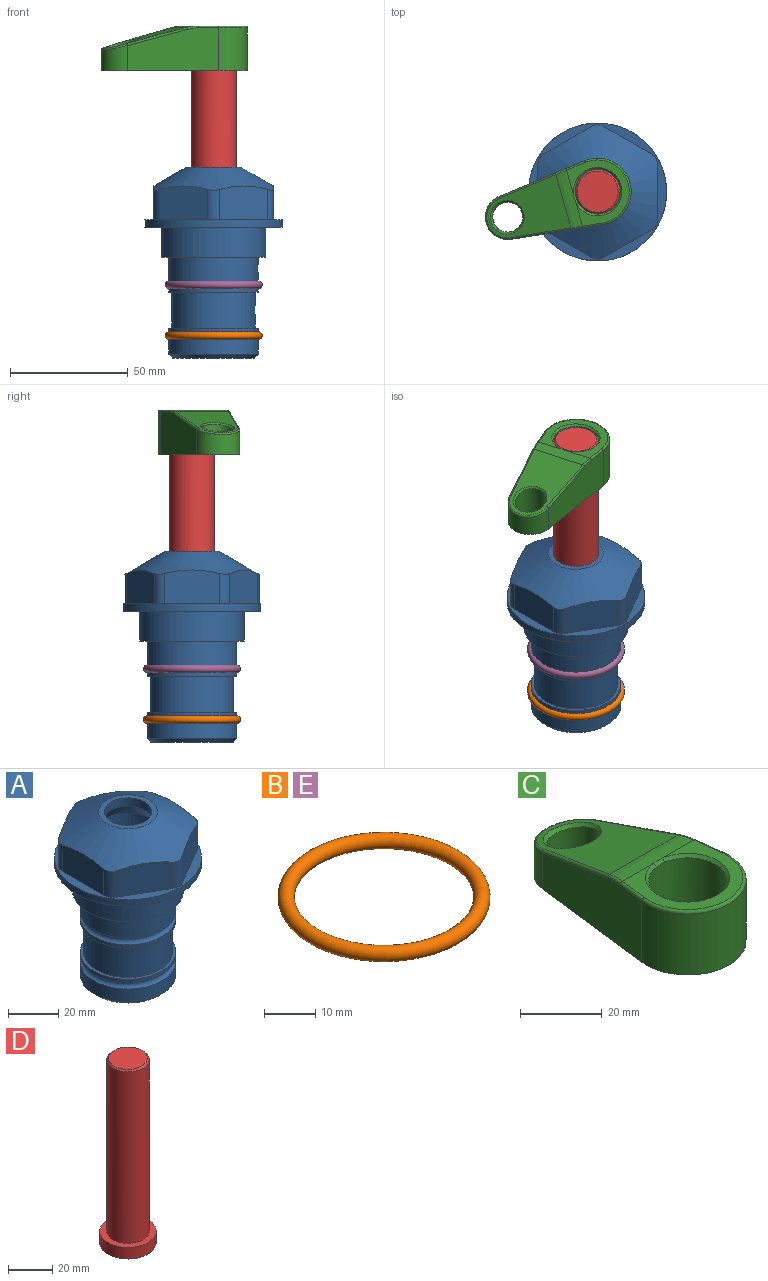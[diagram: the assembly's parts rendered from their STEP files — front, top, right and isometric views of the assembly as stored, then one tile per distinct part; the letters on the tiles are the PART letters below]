
ASSEMBLY  parts=5 mates=4
PART A: 36 faces, bbox 58.7x58.7x81 mm
  f0: cylinder r=17.78mm len=35.56mm, axis (0,0,1), area 1670.8mm2, adj f23,f24,f31
  f1: cylinder r=19.05mm len=38.1mm, axis (0,0,1), area 1191.9mm2, adj f26,f27,f30
  f2: plane 58.66x58.66mm, normal (0,0,-1), area 1150.6mm2, adj f3,f28
  f3: cylinder r=29.33mm len=58.66mm, axis (0,0,-1), area 585.1mm2, adj f2,f4
  f4: plane 58.66x58.66mm, normal (0,0,1), area 475.9mm2, adj f3,f5,f6,f7,f8,f9,f10,f11
  f5: plane 20.32x14.34mm, normal (-0.5,0.87,0), area 324.4mm2, adj f4,f15,f16,f17
  f6: plane 20.32x14.34mm, normal (0.5,0.87,0), area 324.4mm2, adj f4,f14,f15,f17
  f7: plane 23.48x14.34mm, normal (1,0,0), area 324.4mm2, adj f4,f13,f14,f17
  f8: plane 20.32x14.34mm, normal (0.5,-0.87,0), area 324.4mm2, adj f4,f12,f13,f17
  f9: plane 20.32x14.34mm, normal (-0.5,-0.87,0), area 324.4mm2, adj f4,f11,f12,f17
  f10: plane 23.48x14.34mm, normal (-1,0,0), area 324.4mm2, adj f4,f11,f16,f17
  f11: cylinder r=5.08mm len=12.85mm, axis (0,0,-1), area 67.2mm2, adj f4,f9,f10,f17
  f12: cylinder r=5.08mm len=12.85mm, axis (0,0,-1), area 67.2mm2, adj f4,f8,f9,f17
  f13: cylinder r=5.08mm len=12.85mm, axis (0,0,-1), area 67.2mm2, adj f4,f7,f8,f17
  f14: cylinder r=5.08mm len=12.85mm, axis (0,0,-1), area 67.2mm2, adj f4,f6,f7,f17
  f15: cylinder r=5.08mm len=12.85mm, axis (0,0,-1), area 67.2mm2, adj f4,f5,f6,f17
  f16: cylinder r=5.08mm len=12.85mm, axis (0,0,-1), area 67.2mm2, adj f4,f5,f10,f17
  f17: cone r=11.73mm half-angle=60deg, axis (0,0,-1), area 2071.8mm2, adj f5,f6,f7,f8,f9,f10,f11,f12
  f18: plane 23.46x23.46mm, normal (0,0,1), area 147.4mm2, adj f17,f35
  f19: plane 34.93x34.93mm, normal (0,0,-1), area 958mm2, adj f29
  f20: cylinder r=19.05mm len=38.1mm, axis (0,0,1), area 760.1mm2, adj f21,f29
  f21: torus R=19.05mm, axis (0,0,1), area 565.3mm2, adj f20,f22
  f22: cylinder r=19.05mm len=38.1mm, axis (0,0,1), area 190mm2, adj f21,f23
  f23: plane 38.1x38.1mm, normal (0,0,1), area 146.9mm2, adj f0,f22
  f24: plane 38.1x38.1mm, normal (0,0,-1), area 146.9mm2, adj f0,f25
  f25: cylinder r=19.05mm len=38.1mm, axis (0,0,1), area 190mm2, adj f24,f26
  f26: torus R=19.05mm, axis (0,0,1), area 565.3mm2, adj f1,f25
  f27: plane 44.45x44.45mm, normal (0,0,-1), area 411.7mm2, adj f1,f28
  f28: cylinder r=22.23mm len=44.45mm, axis (0,0,1), area 1773.5mm2, adj f2,f27
  f29: cone r=19.05mm half-angle=45deg, axis (0,0,1), area 257.5mm2, adj f19,f20
  f30: cylinder r=3.17mm len=6.75mm, axis (-1,0,0), area 128mm2, adj f1,f33
  f31: cylinder r=3.17mm len=6.35mm, axis (-1,0,0), area 102.5mm2, adj f0,f33
  f32: plane 25.4x25.4mm, normal (0,0,1), area 506.7mm2, adj f33
  f33: cylinder r=12.7mm len=66.42mm, axis (0,0,-1), area 5236.2mm2, adj f30,f31,f32,f34
  f34: cone r=9.53mm half-angle=30deg, axis (0,0,-1), area 443.4mm2, adj f33,f35
  f35: cylinder r=9.53mm len=19.05mm, axis (0,0,-1), area 240.9mm2, adj f18,f34
PART B: 1 faces, bbox 44.7x44.7x3.2 mm
  f0: torus R=19.05mm, axis (0,0,1), area 1193.9mm2
PART C: 31 faces, bbox 31.7x65.5x19.8 mm
  f0: plane 39.12x18.26mm, normal (0.99,0.12,0), area 612.2mm2, adj f1,f4,f7,f11,f13,f15
  f1: cylinder r=9.53mm len=18.91mm, axis (0,0,-1), area 296.1mm2, adj f0,f2,f7,f17
  f2: plane 39.12x18.26mm, normal (-0.99,0.12,0), area 612.2mm2, adj f1,f4,f7,f12,f14,f16
  f3: cylinder r=6.35mm len=12.7mm, axis (0,0,-1), area 362.4mm2, adj f7,f18
  f4: cylinder r=14.29mm len=28.58mm, axis (0,0,-1), area 882.2mm2, adj f0,f2,f7,f10
  f5: cylinder r=9.53mm len=19.05mm, axis (0,0,-1), area 1092.6mm2, adj f7,f19,f20
  f6: plane 26.99x23.69mm, normal (0,0,1), area 216.2mm2, adj f9,f10,f11,f12,f19
  f7: plane 63.5x28.58mm, normal (0,0,-1), area 661.8mm2, adj f0,f1,f2,f3,f4,f5,f22,f23
  f8: plane 33.52x23.6mm, normal (0,0.26,0.97), area 486mm2, adj f9,f15,f16,f17,f18
  f9: cylinder r=19.05mm len=24.72mm, axis (1,0,0), area 120.4mm2, adj f6,f8,f13,f14,f20
  f10: torus R=13.49mm, axis (0,0,1), area 59mm2, adj f4,f6,f11,f12
  f11: cylinder r=0.79mm len=8.67mm, axis (0.12,-0.99,0), area 10.8mm2, adj f0,f6,f10,f13
  f12: cylinder r=0.79mm len=8.67mm, axis (0.12,0.99,0), area 10.8mm2, adj f2,f6,f10,f14
  f13: bspline ~4.95x1.42mm, area 6.1mm2, adj f0,f9,f11,f15
  f14: bspline ~4.95x1.42mm, area 6.1mm2, adj f2,f9,f12,f16
  f15: cylinder r=0.79mm len=25.95mm, axis (0.12,-0.96,0.26), area 32.9mm2, adj f0,f8,f13,f17
  f16: cylinder r=0.79mm len=25.95mm, axis (0.12,0.96,-0.26), area 32.9mm2, adj f2,f8,f14,f17
  f17: bspline ~18.91x8.38mm, area 30mm2, adj f1,f8,f15,f16
  f18: bspline ~14.29x14.29mm, area 48.3mm2, adj f3,f8
  f19: cone r=9.53mm half-angle=45deg, axis (0,0,1), area 66.5mm2, adj f5,f6,f20
  f20: bspline ~3.22x0.96mm, area 3.5mm2, adj f5,f9,f19
  f21: plane 2.75x2.72mm, normal (0,0,-1), area 2.9mm2, adj f23,f25,f28
  f22: plane 23.05x15.88mm, normal (-0.99,-0.12,0), area 323.6mm2, adj f7,f25,f26,f27,f28,f29
  f23: plane 23.05x15.88mm, normal (0.99,-0.12,0), area 323.6mm2, adj f7,f21,f25,f27,f28,f30
  f24: cylinder r=9.53mm len=10.69mm, axis (0,0,-1), area 114.7mm2, adj f7,f27,f29,f30
  f25: cylinder r=12.7mm len=20.59mm, axis (0,0,-1), area 381.1mm2, adj f7,f21,f22,f23,f26,f28
  f26: plane 2.75x2.72mm, normal (0,0,-1), area 2.9mm2, adj f22,f25,f28
  f27: plane 19.72x18.37mm, normal (0,-0.26,-0.97), area 291.8mm2, adj f22,f23,f24,f28,f29,f30
  f28: cylinder r=15.88mm len=19.92mm, axis (1,0,0), area 54.8mm2, adj f21,f22,f23,f25,f26,f27
  f29: cylinder r=1.59mm len=11mm, axis (0,0,-1), area 34.7mm2, adj f7,f22,f24,f27
  f30: cylinder r=1.59mm len=11mm, axis (0,0,-1), area 34.7mm2, adj f7,f23,f24,f27
PART D: 6 faces, bbox 25.4x25.4x101.6 mm
  f0: plane 17.46x17.46mm, normal (0,0,1), area 239.5mm2, adj f5
  f1: plane 25.4x25.4mm, normal (0,0,-1), area 506.7mm2, adj f2
  f2: cylinder r=12.7mm len=25.4mm, axis (0,0,1), area 506.7mm2, adj f1,f3
  f3: plane 25.4x25.4mm, normal (0,0,1), area 221.7mm2, adj f2,f4
  f4: cylinder r=9.53mm len=94.46mm, axis (0,0,1), area 5653mm2, adj f3,f5
  f5: cone r=8.73mm half-angle=45deg, axis (0,0,-1), area 64.4mm2, adj f0,f4
PART E: same geometry as B
PLACE A at identity fixed
PLACE B t=(0,0,-21.59)mm
PLACE C rot(axis=(0,0,1),105.8deg) t=(0,0,22)mm
PLACE D rot(axis=(0,0,1),105.8deg) t=(0,0,21.2)mm
PLACE E at identity
MATE cylindrical A.f0 <-> D.f2  axis (0,0,1) through (0,0,-50.55)mm
MATE fastened B.f0 <-> A.f0  axis (0,0,1) through (0,0,-46.1)mm
MATE fastened E.f0 <-> A.f0  axis (0,0,1) through (0,0,-24.51)mm
MATE fastened D.f2 <-> C.f4  axis (0,0,1) through (0,0,84.7)mm
